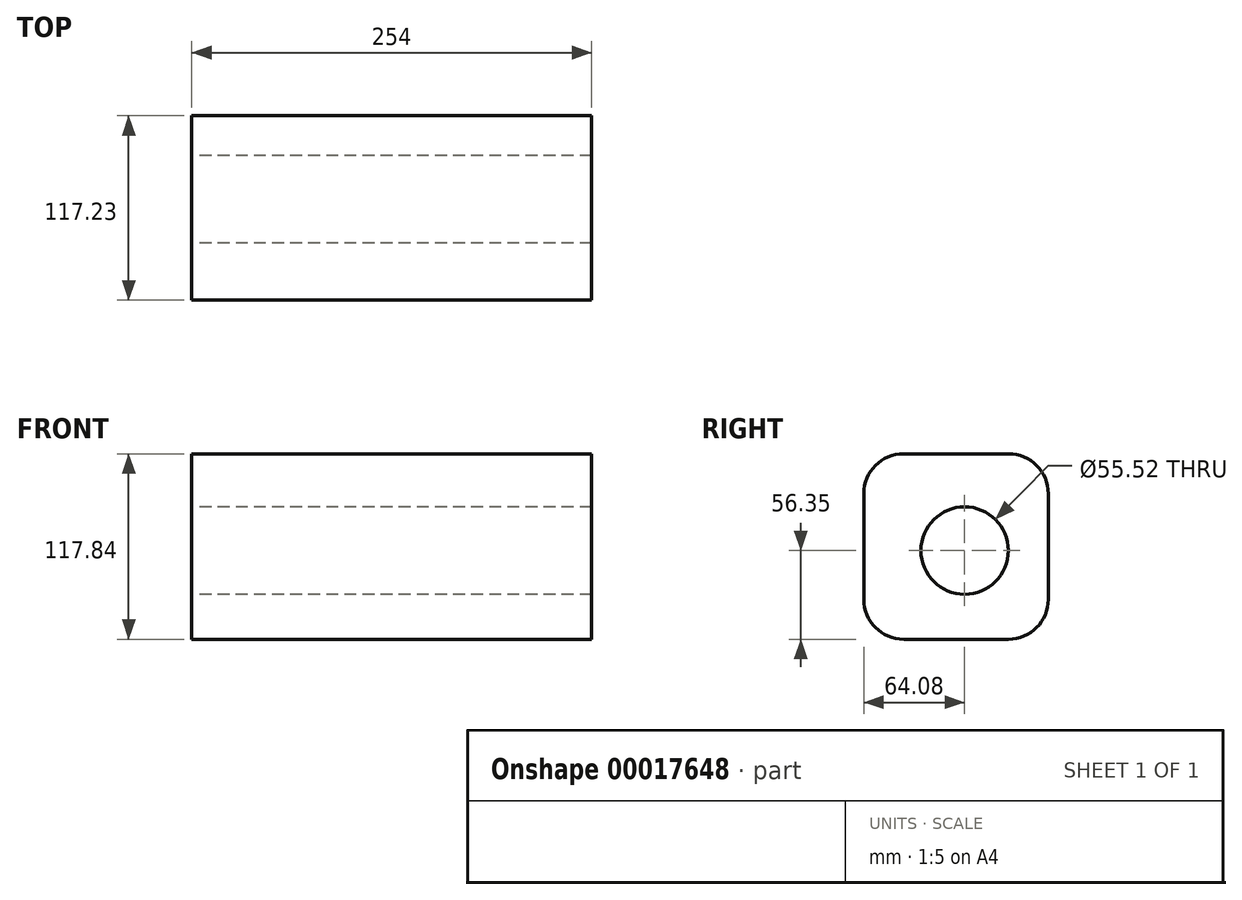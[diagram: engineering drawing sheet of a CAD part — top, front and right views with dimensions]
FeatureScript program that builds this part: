
annotation { "Feature Type Name" : "Feature", "Feature Type Description" : "" }
export const myFeature = defineFeature(function(context is Context, id is Id, definition is map)
    precondition{}
    {
        {
            var Q0;
            Q0=qCreatedBy(makeId("Right.planeOp"),FACE);
            var sketch = newSketch(context, id + "F0", { "sketchPlane" : qUnion([Q0])});
            skLineSegment(sketch, "E0.bottom", {"start": v(-38.68, -56.35) * mm, "end": v(27.75, -56.35) * mm});
            skLineSegment(sketch, "E0.top", {"start": v(-38.68, 61.5) * mm, "end": v(27.75, 61.5) * mm});
            skLineSegment(sketch, "E0.left", {"start": v(-64.08, -30.95) * mm, "end": v(-64.08, 36.1) * mm});
            skLineSegment(sketch, "E0.right", {"start": v(53.15, -30.95) * mm, "end": v(53.15, 36.1) * mm});
            skCircle(sketch, "E1", {"center": v(0, 0) * mm, "radius": 27.76 * mm});
            skPoint(sketch, "E2.visualSharp", {"position": v(-64.08, 61.5) * mm});
            skArc(sketch, "E2.filletArc", {"start": v(-38.68, 61.5) * mm, "mid": v(-56.64, 54.05) * mm, "end": v(-64.08, 36.1) * mm});
            skPoint(sketch, "E3.visualSharp", {"position": v(53.15, 61.5) * mm});
            skArc(sketch, "E3.filletArc", {"start": v(53.15, 36.1) * mm, "mid": v(45.71, 54.05) * mm, "end": v(27.75, 61.5) * mm});
            skPoint(sketch, "E4.visualSharp", {"position": v(53.15, -56.35) * mm});
            skArc(sketch, "E4.filletArc", {"start": v(27.75, -56.35) * mm, "mid": v(45.71, -48.92) * mm, "end": v(53.15, -30.95) * mm});
            skPoint(sketch, "E5.visualSharp", {"position": v(-64.08, -56.35) * mm});
            skArc(sketch, "E5.filletArc", {"start": v(-64.08, -30.95) * mm, "mid": v(-56.64, -48.92) * mm, "end": v(-38.68, -56.35) * mm});
            skSolve(sketch);
        }
        {
            var Q0;
            Q0=makeQuery(id+"F0.imprint","IMPRINT",FACE,{"disambiguationData":[TD([[makeQuery(id+"F0.imprint","IMPRINT",EDGE,{"derivedFrom":sQuery(id+"F0.wireOp",EDGE,"E0.bottom")}),1.0]])]});
            extrude(context, id + "F1", {"entities" : qUnion([Q0]), "depth" : 254 * mm});
        }
    });
